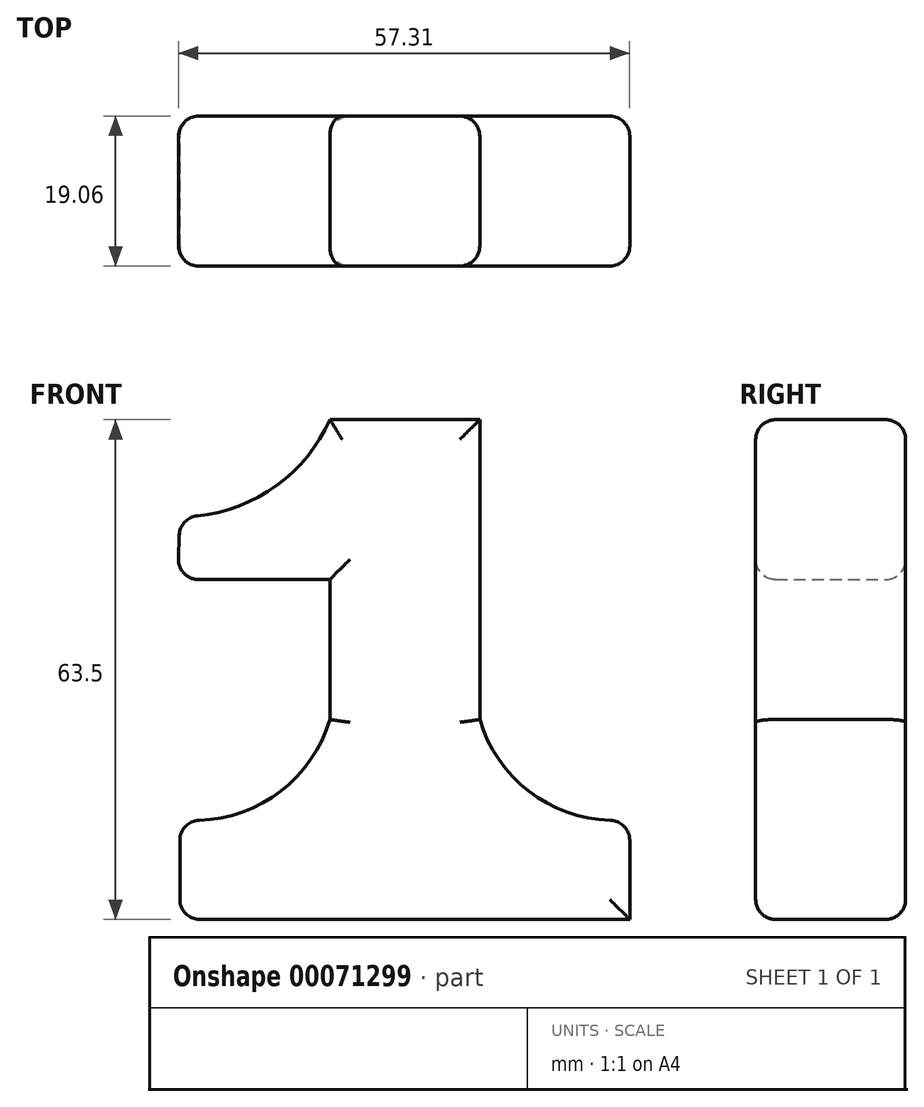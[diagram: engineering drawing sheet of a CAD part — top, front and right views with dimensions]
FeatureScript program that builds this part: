
annotation { "Feature Type Name" : "Feature", "Feature Type Description" : "" }
export const myFeature = defineFeature(function(context is Context, id is Id, definition is map)
    precondition{}
    {
        {
            var Q0;
            Q0=qCreatedBy(makeId("Front.planeOp"),FACE);
            var sketch = newSketch(context, id + "F0", { "sketchPlane" : qUnion([Q0])});
            skLineSegment(sketch, "E0.rect.bottom", {"start": v(19.05, -63.5) * mm, "end": v(-19.05, -63.5) * mm});
            skLineSegment(sketch, "E0.rect.top", {"start": v(19.05, 63.5) * mm, "end": v(-19.05, 63.5) * mm});
            skLineSegment(sketch, "E0.rect.left", {"start": v(19.05, -63.5) * mm, "end": v(19.05, 63.5) * mm});
            skLineSegment(sketch, "E0.rect.right", {"start": v(-19.05, -63.5) * mm, "end": v(-19.05, 63.5) * mm});
            skPoint(sketch, "E0.rect.middle", {"position": v(0, 0) * mm});
            skPoint(sketch, "E1", {"position": v(0, -63.5) * mm});
            skLineSegment(sketch, "E2", {"start": v(19.05, -63.5) * mm, "end": v(57.15, -63.5) * mm});
            skLineSegment(sketch, "E3", {"start": v(-19.05, -63.5) * mm, "end": v(-57.15, -63.5) * mm});
            skLineSegment(sketch, "E4", {"start": v(-57.15, -63.5) * mm, "end": v(-57.15, -38.1) * mm});
            skLineSegment(sketch, "E5", {"start": v(57.15, -63.5) * mm, "end": v(57.15, -38.1) * mm});
            skArc(sketch, "E6", {"start": v(-57.15, -38.1) * mm, "mid": v(-33.47, -32.35) * mm, "end": v(-19.05, -12.7) * mm});
            skArc(sketch, "E7", {"start": v(19.05, -12.7) * mm, "mid": v(33.47, -32.35) * mm, "end": v(57.15, -38.1) * mm});
            skArc(sketch, "E8", {"start": v(-57.15, 38.82) * mm, "mid": v(-34.41, 45.47) * mm, "end": v(-19.05, 63.5) * mm});
            skLineSegment(sketch, "E9", {"start": v(-19.05, 22.86) * mm, "end": v(-57.65, 22.86) * mm});
            skLineSegment(sketch, "E10", {"start": v(-57.65, 22.86) * mm, "end": v(-57.15, 38.82) * mm});
            skSolve(sketch);
        }
        {
            var Q0;
            {var subQ3=sQuery(id+"F0.wireOp",EDGE,"E0.rect.bottom");Q0=makeQuery(id+"F0.imprint","IMPRINT",FACE,{"disambiguationData":[TD([[makeQuery(id+"F0.imprint","IMPRINT",EDGE,{"derivedFrom":subQ3}),-1.0]])]});}
            var Q1;
            {var subQ0=sQuery(id+"F0.wireOp",EDGE,"E8");Q1=makeQuery(id+"F0.imprint","IMPRINT",FACE,{"disambiguationData":[TD([[makeQuery(id+"F0.imprint","IMPRINT",EDGE,{"derivedFrom":subQ0}),-1.0]])]});}
            var Q2;
            {var subQ0=sQuery(id+"F0.wireOp",EDGE,"E2");Q2=makeQuery(id+"F0.imprint","IMPRINT",FACE,{"disambiguationData":[TD([[makeQuery(id+"F0.imprint","IMPRINT",EDGE,{"derivedFrom":subQ0}),1.0]])]});}
            var Q3;
            {var subQ0=sQuery(id+"F0.wireOp",EDGE,"E3");Q3=makeQuery(id+"F0.imprint","IMPRINT",FACE,{"disambiguationData":[TD([[makeQuery(id+"F0.imprint","IMPRINT",EDGE,{"derivedFrom":subQ0}),-1.0]])]});}
            extrude(context, id + "F1", {"entities" : qUnion([Q0, Q1, Q2, Q3]), "endBound" : BoundingType.SYMMETRIC, "depth" : 38.1 * mm});
        }
        {
            var Q0;
            Q0=makeQuery(id+"F1.opExtrude","CAP_EDGE",EDGE,{"disambiguationData":[OSD([sQuery(id+"F0.wireOp",EDGE,"E0.rect.left")])],"isStart":false});
            var Q1;
            Q1=makeQuery(id+"F1.opExtrude","CAP_EDGE",EDGE,{"disambiguationData":[OSD([sQuery(id+"F0.wireOp",EDGE,"E7")])],"isStart":false});
            var Q2;
            Q2=makeQuery(id+"F1.opExtrude","CAP_EDGE",EDGE,{"disambiguationData":[OSD([sQuery(id+"F0.wireOp",EDGE,"E7")])],"isStart":true});
            var Q3;
            Q3=makeQuery(id+"F1.opExtrude","CAP_EDGE",EDGE,{"disambiguationData":[OSD([sQuery(id+"F0.wireOp",EDGE,"E0.rect.left")])],"isStart":true});
            var Q4;
            Q4=makeQuery(id+"F1.opExtrude","SWEPT_EDGE",EDGE,{"disambiguationData":[OSD([sQuery(id+"F0.wireOp",EDGE,"E5"),sQuery(id+"F0.wireOp",EDGE,"E7")])]});
            var Q5;
            Q5=makeQuery(id+"F1.opExtrude","CAP_EDGE",EDGE,{"disambiguationData":[OSD([sQuery(id+"F0.wireOp",EDGE,"E0.rect.top")])],"isStart":false});
            var Q6;
            Q6=makeQuery(id+"F1.opExtrude","CAP_EDGE",EDGE,{"disambiguationData":[OSD([sQuery(id+"F0.wireOp",EDGE,"E0.rect.top")])],"isStart":true});
            var Q7;
            Q7=makeQuery(id+"F1.opExtrude","CAP_EDGE",EDGE,{"disambiguationData":[OSD([sQuery(id+"F0.wireOp",EDGE,"E8")])],"isStart":false});
            var Q8;
            Q8=makeQuery(id+"F1.opExtrude","CAP_EDGE",EDGE,{"disambiguationData":[OSD([sQuery(id+"F0.wireOp",EDGE,"E8")])],"isStart":true});
            var Q9;
            Q9=makeQuery(id+"F1.opExtrude","CAP_EDGE",EDGE,{"disambiguationData":[OSD([sQuery(id+"F0.wireOp",EDGE,"E0.rect.right")])],"isStart":true});
            var Q10;
            Q10=makeQuery(id+"F1.opExtrude","CAP_EDGE",EDGE,{"disambiguationData":[OSD([sQuery(id+"F0.wireOp",EDGE,"E6")])],"isStart":true});
            var Q11;
            Q11=makeQuery(id+"F1.opExtrude","CAP_EDGE",EDGE,{"disambiguationData":[OSD([sQuery(id+"F0.wireOp",EDGE,"E9")])],"isStart":true});
            var Q12;
            Q12=makeQuery(id+"F1.opExtrude","CAP_EDGE",EDGE,{"disambiguationData":[OSD([sQuery(id+"F0.wireOp",EDGE,"E9")])],"isStart":false});
            var Q13;
            Q13=makeQuery(id+"F1.opExtrude","CAP_EDGE",EDGE,{"disambiguationData":[OSD([sQuery(id+"F0.wireOp",EDGE,"E0.rect.right")])],"isStart":false});
            var Q14;
            Q14=makeQuery(id+"F1.opExtrude","CAP_EDGE",EDGE,{"disambiguationData":[OSD([sQuery(id+"F0.wireOp",EDGE,"E6")])],"isStart":false});
            var Q15;
            Q15=makeQuery(id+"F1.opExtrude","CAP_EDGE",EDGE,{"disambiguationData":[OSD([sQuery(id+"F0.wireOp",EDGE,"E0.rect.bottom"),sQuery(id+"F0.wireOp",EDGE,"E2"),sQuery(id+"F0.wireOp",EDGE,"E3")])],"isStart":false});
            var Q16;
            Q16=makeQuery(id+"F1.opExtrude","CAP_EDGE",EDGE,{"disambiguationData":[OSD([sQuery(id+"F0.wireOp",EDGE,"E4")])],"isStart":false});
            var Q17;
            Q17=makeQuery(id+"F1.opExtrude","CAP_EDGE",EDGE,{"disambiguationData":[OSD([sQuery(id+"F0.wireOp",EDGE,"E5")])],"isStart":false});
            var Q18;
            Q18=makeQuery(id+"F1.opExtrude","CAP_EDGE",EDGE,{"disambiguationData":[OSD([sQuery(id+"F0.wireOp",EDGE,"E4")])],"isStart":true});
            var Q19;
            Q19=makeQuery(id+"F1.opExtrude","CAP_EDGE",EDGE,{"disambiguationData":[OSD([sQuery(id+"F0.wireOp",EDGE,"E0.rect.bottom"),sQuery(id+"F0.wireOp",EDGE,"E2"),sQuery(id+"F0.wireOp",EDGE,"E3")])],"isStart":true});
            var Q20;
            Q20=makeQuery(id+"F1.opExtrude","CAP_EDGE",EDGE,{"disambiguationData":[OSD([sQuery(id+"F0.wireOp",EDGE,"E5")])],"isStart":true});
            var Q21;
            Q21=makeQuery(id+"F1.opExtrude","SWEPT_EDGE",EDGE,{"disambiguationData":[OSD([sQuery(id+"F0.wireOp",EDGE,"E3"),sQuery(id+"F0.wireOp",EDGE,"E4")])]});
            var Q22;
            Q22=makeQuery(id+"F1.opExtrude","SWEPT_EDGE",EDGE,{"disambiguationData":[OSD([sQuery(id+"F0.wireOp",EDGE,"E4"),sQuery(id+"F0.wireOp",EDGE,"E6")])]});
            var Q23;
            Q23=makeQuery(id+"F1.opExtrude","SWEPT_FACE",FACE,{"disambiguationData":[OSD([sQuery(id+"F0.wireOp",EDGE,"E10")])]});
            fillet(context, id + "F2", {"entities" : qUnion([Q0, Q1, Q2, Q3, Q4, Q5, Q6, Q7, Q8, Q9, Q10, Q11, Q12, Q13, Q14, Q15, Q16, Q17, Q18, Q19, Q20, Q21, Q22, Q23]), "radius" : 5.08 * mm, "tangentPropagation" : true, "allowEdgeOverflow" : false});
        }
        {
            var Q0;
            Q0=makeQuery(id+"F1.opExtrude","SWEPT_BODY",BODY,{"disambiguationData":[OSD([sQuery(id+"F0.wireOp",EDGE,"E0.rect.bottom"),sQuery(id+"F0.wireOp",EDGE,"E0.rect.top"),sQuery(id+"F0.wireOp",EDGE,"E0.rect.left"),sQuery(id+"F0.wireOp",EDGE,"E0.rect.right"),sQuery(id+"F0.wireOp",EDGE,"E2"),sQuery(id+"F0.wireOp",EDGE,"E3"),sQuery(id+"F0.wireOp",EDGE,"E4"),sQuery(id+"F0.wireOp",EDGE,"E5"),sQuery(id+"F0.wireOp",EDGE,"E6"),sQuery(id+"F0.wireOp",EDGE,"E7"),sQuery(id+"F0.wireOp",EDGE,"E8"),sQuery(id+"F0.wireOp",EDGE,"E9"),sQuery(id+"F0.wireOp",EDGE,"E10")])]});
            var Q1;
            Q1=qCreatedBy(makeId("Origin.pointOp"),VERTEX);
            transform(context, id + "F3", {"entities" : qUnion([Q0]), "transformType" : TransformType.SCALE_UNIFORMLY, "scale" : 0.5, "scalePoint" : qUnion([Q1]), "makeCopy" : false});
        }
    });
